# Revit family: KingswayGroup_DrStps_Anti-LigatureSwingStopAnti-BarricadeDoorStop
name_source: partatom
category: Specialty Equipment
units: mm (PartAtom-declared; Revit-internal decimal feet)

## family parameters
Always vertical = No
Cut with Voids When Loaded = No
Part Type = Normal
Room Calculation Point = No
Round Connector Dimension = Use Diameter
Shared = No
Work Plane-Based = No

## types (1)
- KingswayGroup_DrStps_Anti-LigatureSwingStopAnti-BarricadeDoorStop
    AssetType = Fixed
    BIMObjectName = KingswayGroup_DoorStops_Anti-LigatureSwingStopAnti-BarricadeDoorStop
    CapMaterial = NBS_Concept
    Category = Pr_30_36_33_24:Door stops
    Color = For full range of available finishes and colours, contact Kingsway Group
    Default Elevation = 0 mm  [stored 0 ft]
    Description = SwingStop 2 Lock, Hardwood Stop
    DurationUnit = year
    Features = The KG205 SwingStop provides single-action use to double-action doors when locked by preventing the door leaf from opening outwards
    Finish = For full range of available finishes and colours, contact Kingsway Group
    IfcExportAs = IfcDiscreteAccessoryType
    IfcExportType = USERDEFINED
    Manufacturer = Kingsway Group
    ManufacturerName = Kingsway Group
    ManufacturerURL = https://kingswaygroupglobal.com
    Material = Ash, Beech, Oak
    Model = KG205
    ModelNumber = KG205
    ModelReference = Anti-Ligature SwingStop Anti-Barricade Door Stop, 2 Point Lock, Hardwood
    Name = DoorStops_Anti-LigatureSwingStopAnti-BarricadeDoorStop_KG205_KingswayGroup
    NominalHeight = 2108 mm  [stored 6.91601 ft]
    NominalLength = 67 mm
    NominalWidth = 47 mm  [stored 0.154199 ft]
    PlateMaterial = NBS_Concept
    ProductInformation = https://kingswaygroupglobal.com
    Size = 67 x 2108 x 47 mm
    TimberMaterial = NBS_Concept
    URL = https://kingswaygroupglobal.com
    Uniclass2015Code = Pr_30_36_33_24
    Uniclass2015Title = Door stops
    Uniclass2015Version = Products v1.36
    Version = 1
    WarrantyDescription = 5-Year Guarantee *For faulty manufacture and not for damage
    WarrantyDurationParts = 5
    WarrantyDurationUnit = year

note: [stored X ft] marks values corroborated as IEEE doubles in the binary element streams (Revit-internal decimal feet)

## geometry (parser evidence)
native form markers: Sweep x2
no freeform markers — native parametric forms only
